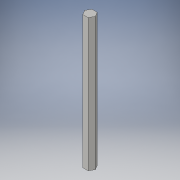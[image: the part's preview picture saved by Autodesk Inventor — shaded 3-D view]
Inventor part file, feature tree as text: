
AUTODESK INVENTOR PART (.ipt)
format: ipt  version: 2016 (Build 200138000, 138)  size: 91,648 bytes
history: native  units: in
note: dims shown in document units (in); Inventor stores cm internally (conversion verified against a paired STEP export)
features: extrude x1, sketch x1
ambient origin geometry x8: Origin, YZ Plane, XZ Plane, XY Plane, X Axis, Y Axis, Z Axis, Center Point
bodies: Solid1 (feature_tree)
feature tree (2):
  extrude  "Extrusion1"  Depth=7.25in TaperAngle=0.0deg
  sketch  "Sketch1"  dims[d0=0.5in d1=7.25in d2=0.0in]
